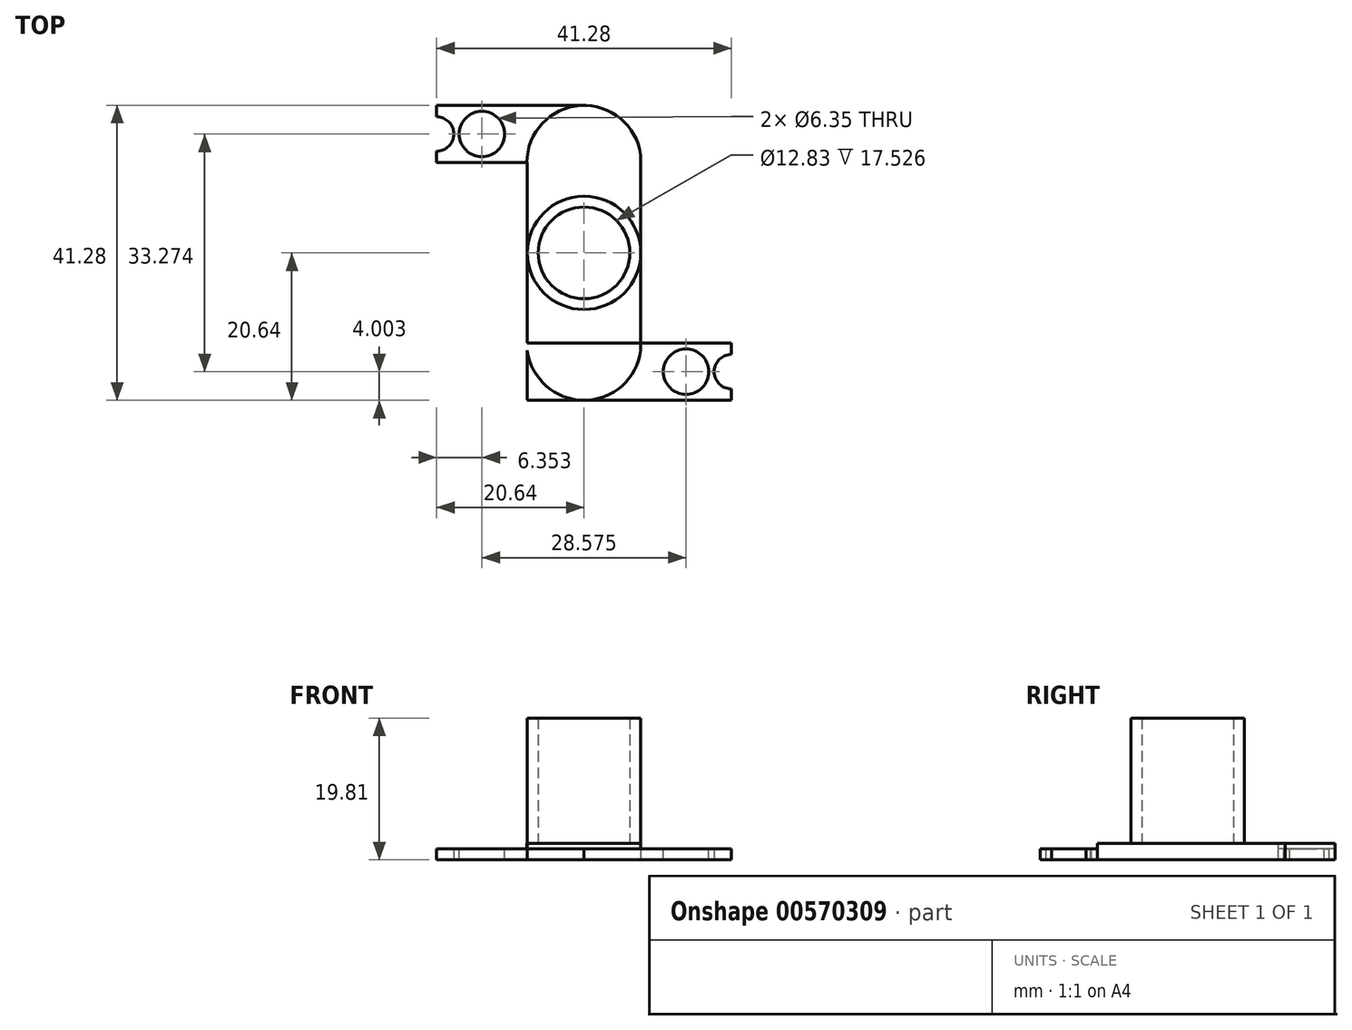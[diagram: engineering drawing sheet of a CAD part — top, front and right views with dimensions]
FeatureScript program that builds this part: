
annotation { "Feature Type Name" : "Feature", "Feature Type Description" : "" }
export const myFeature = defineFeature(function(context is Context, id is Id, definition is map)
    precondition{}
    {
        {
            var Q0;
            Q0=qCreatedBy(makeId("Top.planeOp"),FACE);
            var sketch = newSketch(context, id + "F0", { "sketchPlane" : qUnion([Q0])});
            skLineSegment(sketch, "E0.bottom", {"start": v(20.64, 20.64) * mm, "end": v(-20.64, 20.64) * mm});
            skLineSegment(sketch, "E0.left", {"start": v(20.64, 20.64) * mm, "end": v(20.64, -20.64) * mm});
            skLineSegment(sketch, "E0.right", {"start": v(-20.64, 20.64) * mm, "end": v(-20.64, -20.64) * mm});
            skPoint(sketch, "E0.middle", {"position": v(0, 0) * mm});
            skLineSegment(sketch, "E1.bottom", {"start": v(7.94, 20.64) * mm, "end": v(-7.94, 20.64) * mm});
            skLineSegment(sketch, "E1.top", {"start": v(7.94, -20.64) * mm, "end": v(-7.94, -20.64) * mm});
            skLineSegment(sketch, "E1.left", {"start": v(7.94, 20.64) * mm, "end": v(7.94, -20.64) * mm});
            skLineSegment(sketch, "E1.right", {"start": v(-7.94, 20.64) * mm, "end": v(-7.94, -20.64) * mm});
            skLineSegment(sketch, "E2.bottom", {"start": v(-20.64, 20.64) * mm, "end": v(20.64, 20.64) * mm});
            skLineSegment(sketch, "E2.top", {"start": v(-20.64, 12.64) * mm, "end": v(20.64, 12.64) * mm});
            skLineSegment(sketch, "E2.left", {"start": v(-20.64, 20.64) * mm, "end": v(-20.64, 12.64) * mm});
            skLineSegment(sketch, "E2.right", {"start": v(20.64, 20.64) * mm, "end": v(20.64, 12.64) * mm});
            skLineSegment(sketch, "E3.top", {"start": v(-20.64, -12.64) * mm, "end": v(20.64, -12.64) * mm});
            skLineSegment(sketch, "E3.left", {"start": v(-20.64, -20.64) * mm, "end": v(-20.64, -12.64) * mm});
            skLineSegment(sketch, "E3.right", {"start": v(20.64, -20.64) * mm, "end": v(20.64, -12.64) * mm});
            skArc(sketch, "E4", {"start": v(0, 20.64) * mm, "mid": v(-5.29, 18.64) * mm, "end": v(-7.94, 13.64) * mm});
            skArc(sketch, "E5", {"start": v(0, 20.64) * mm, "mid": v(5.29, 18.64) * mm, "end": v(7.94, 13.64) * mm});
            skArc(sketch, "E6", {"start": v(0, -20.64) * mm, "mid": v(-5.29, -18.64) * mm, "end": v(-7.94, -13.64) * mm});
            skArc(sketch, "E7", {"start": v(0, -20.64) * mm, "mid": v(5.29, -18.64) * mm, "end": v(7.94, -13.64) * mm});
            skLineSegment(sketch, "E8", {"start": v(0, -20.64) * mm, "end": v(20.64, -20.64) * mm});
            skCircle(sketch, "E9", {"center": v(20.64, -16.64) * mm, "radius": 2.41 * mm});
            skCircle(sketch, "E10", {"center": v(-20.64, 16.64) * mm, "radius": 2.41 * mm});
            skSolve(sketch);
        }
        {
            var Q0;
            {var subQ3=sQuery(id+"F0.wireOp",EDGE,"E1.right");var subQ9=sQuery(id+"F0.wireOp",EDGE,"E2.bottom");var subQ10=makeQuery(id+"F0.imprint","INTERSECT",VERTEX,{"derivedFrom":[subQ3,subQ9]});Q0=makeQuery(id+"F0.imprint","IMPRINT",FACE,{"disambiguationData":[TD([[makeQuery(id+"F0.imprint","IMPRINT",EDGE,{"disambiguationData":[TD([[subQ10,-1.0]])],"derivedFrom":subQ3}),-1.0]])]});}
            var Q1;
            {var subQ3=sQuery(id+"F0.wireOp",EDGE,"E4");Q1=makeQuery(id+"F0.imprint","IMPRINT",FACE,{"disambiguationData":[TD([[makeQuery(id+"F0.imprint","IMPRINT",EDGE,{"derivedFrom":subQ3}),-1.0]])]});}
            var Q2;
            {var subQ0=sQuery(id+"F0.wireOp",EDGE,"E4");Q2=makeQuery(id+"F0.imprint","IMPRINT",FACE,{"disambiguationData":[TD([[makeQuery(id+"F0.imprint","IMPRINT",EDGE,{"derivedFrom":subQ0}),1.0]])]});}
            var Q3;
            {var subQ0=sQuery(id+"F0.wireOp",EDGE,"E2.top");var subQ1=sQuery(id+"F0.wireOp",EDGE,"E1.left");var subQ2=makeQuery(id+"F0.imprint","INTERSECT",VERTEX,{"derivedFrom":[subQ1,subQ0]});Q3=makeQuery(id+"F0.imprint","IMPRINT",FACE,{"disambiguationData":[TD([[makeQuery(id+"F0.imprint","IMPRINT",EDGE,{"disambiguationData":[TD([[subQ2,-1.0]])],"derivedFrom":subQ1}),-1.0]])]});}
            var Q4;
            {var subQ0=sQuery(id+"F0.wireOp",EDGE,"E6");Q4=makeQuery(id+"F0.imprint","IMPRINT",FACE,{"disambiguationData":[TD([[makeQuery(id+"F0.imprint","IMPRINT",EDGE,{"derivedFrom":subQ0}),-1.0]])]});}
            var Q5;
            {var subQ3=sQuery(id+"F0.wireOp",EDGE,"E7");Q5=makeQuery(id+"F0.imprint","IMPRINT",FACE,{"disambiguationData":[TD([[makeQuery(id+"F0.imprint","IMPRINT",EDGE,{"derivedFrom":subQ3}),-1.0]])]});}
            var Q6;
            {var subQ7=sQuery(id+"F0.wireOp",EDGE,"E1.left");var subQ10=makeQuery(id+"F0.imprint","INTERSECT",VERTEX,{"derivedFrom":[subQ7,sQuery(id+"F0.wireOp",EDGE,"E7")]});Q6=makeQuery(id+"F0.imprint","IMPRINT",FACE,{"disambiguationData":[TD([[makeQuery(id+"F0.imprint","IMPRINT",EDGE,{"disambiguationData":[TD([[subQ10,1.0]])],"derivedFrom":subQ7}),1.0]])]});}
            extrude(context, id + "F1", {"entities" : qUnion([Q0, Q1, Q2, Q3, Q4, Q5, Q6]), "depth" : 1.52 * mm, "offsetDistance" : 25.4 * mm});
        }
        {
            var Q0;
            Q0=makeQuery(id+"F1.opExtrude","CAP_FACE",FACE,{"disambiguationData":[OSD([sQuery(id+"F0.wireOp",EDGE,"E1.left"),sQuery(id+"F0.wireOp",EDGE,"E1.right"),sQuery(id+"F0.wireOp",EDGE,"E2.bottom"),sQuery(id+"F0.wireOp",EDGE,"E2.top"),sQuery(id+"F0.wireOp",EDGE,"E3.top"),sQuery(id+"F0.wireOp",EDGE,"E3.right"),sQuery(id+"F0.wireOp",EDGE,"E5"),sQuery(id+"F0.wireOp",EDGE,"E6"),sQuery(id+"F0.wireOp",EDGE,"E8"),sQuery(id+"F0.wireOp",EDGE,"E9"),sQuery(id+"F0.wireOp",EDGE,"E2.left"),sQuery(id+"F0.wireOp",EDGE,"E10")])],"isStart":false});
            var sketch = newSketch(context, id + "F2", { "sketchPlane" : qUnion([Q0])});
            skArc(sketch, "E11", {"start": v(0, 20.64) * mm, "mid": v(-5.66, 18.3) * mm, "end": v(-8, 12.64) * mm});
            skArc(sketch, "E12", {"start": v(0, -20.64) * mm, "mid": v(5.66, -18.3) * mm, "end": v(8, -12.64) * mm});
            skSolve(sketch);
        }
        {
            var Q0;
            {var subQ3=sQuery(id+"F2.wireOp",EDGE,"E11");Q0=makeQuery(id+"F2.imprint","IMPRINT",FACE,{"disambiguationData":[TD([[makeQuery(id+"F2.imprint","IMPRINT",EDGE,{"derivedFrom":subQ3}),1.0]])]});}
            extrude(context, id + "F3", {"entities" : qUnion([Q0]), "operationType" : NewBodyOperationType.ADD, "depth" : 0.76 * mm, "offsetDistance" : 25.4 * mm});
        }
        {
            var Q0;
            Q0=makeQuery(id+"F3.opExtrude","CAP_FACE",FACE,{"disambiguationData":[OSD([sQuery(id+"F0.wireOp",EDGE,"E1.left"),sQuery(id+"F0.wireOp",EDGE,"E1.right"),sQuery(id+"F0.wireOp",EDGE,"E2.top"),sQuery(id+"F0.wireOp",EDGE,"E3.top"),sQuery(id+"F0.wireOp",EDGE,"E5"),sQuery(id+"F0.wireOp",EDGE,"E6"),sQuery(id+"F2.wireOp",EDGE,"E11"),sQuery(id+"F2.wireOp",EDGE,"E12")])],"isStart":false});
            var sketch = newSketch(context, id + "F4", { "sketchPlane" : qUnion([Q0])});
            skCircle(sketch, "E13", {"center": v(0, 0) * mm, "radius": 7.94 * mm});
            skCircle(sketch, "E14", {"center": v(0, 0) * mm, "radius": 6.41 * mm});
            skSolve(sketch);
        }
        {
            var Q0;
            Q0=makeQuery(id+"F4.imprint","IMPRINT",FACE,{"disambiguationData":[TD([[makeQuery(id+"F4.imprint","IMPRINT",EDGE,{"derivedFrom":sQuery(id+"F4.wireOp",EDGE,"E14")}),-1.0]])]});
            extrude(context, id + "F5", {"entities" : qUnion([Q0]), "operationType" : NewBodyOperationType.ADD, "depth" : 17.53 * mm, "offsetDistance" : 25.4 * mm});
        }
        {
            var Q0;
            {var subQ0=sQuery(id+"F0.wireOp",EDGE,"E2.left");var subQ1=sQuery(id+"F0.wireOp",EDGE,"E2.bottom");var subQ2=sQuery(id+"F0.wireOp",EDGE,"E10");var subQ3=sQuery(id+"F0.wireOp",EDGE,"E2.top");var subQ4=sQuery(id+"F0.wireOp",EDGE,"E5");Q0=makeQuery(id+"F3.boolean.opBoolean","SPLIT",FACE,{"disambiguationData":[TD([makeQuery(id+"F1.opExtrude","SWEPT_FACE",FACE,{"disambiguationData":[OSD([subQ1])]})])],"derivedFrom":makeQuery(id+"F1.opExtrude","CAP_FACE",FACE,{"disambiguationData":[OSD([sQuery(id+"F0.wireOp",EDGE,"E1.left"),sQuery(id+"F0.wireOp",EDGE,"E1.right"),subQ1,subQ3,sQuery(id+"F0.wireOp",EDGE,"E3.top"),sQuery(id+"F0.wireOp",EDGE,"E3.right"),subQ4,sQuery(id+"F0.wireOp",EDGE,"E6"),sQuery(id+"F0.wireOp",EDGE,"E8"),sQuery(id+"F0.wireOp",EDGE,"E9"),subQ0,subQ2])],"isStart":false})});}
            var sketch = newSketch(context, id + "F6", { "sketchPlane" : qUnion([Q0])});
            skLineSegment(sketch, "E15", {"start": v(-20.64, 20.64) * mm, "end": v(-14.29, 20.64) * mm});
            skLineSegment(sketch, "E16", {"start": v(-14.29, 20.64) * mm, "end": v(-14.29, 12.64) * mm});
            skCircle(sketch, "E17", {"center": v(-14.29, 16.64) * mm, "radius": 3.18 * mm});
            skSolve(sketch);
        }
        {
            var Q0;
            {var subQ7=sQuery(id+"F6.wireOp",EDGE,"E15");Q0=makeQuery(id+"F6.imprint","IMPRINT",FACE,{"disambiguationData":[TD([[makeQuery(id+"F6.imprint","IMPRINT",EDGE,{"derivedFrom":subQ7}),-1.0]])]});}
            var Q1;
            {var subQ0=sQuery(id+"F6.wireOp",EDGE,"E17");var subQ1=sQuery(id+"F6.wireOp",EDGE,"E16");var subQ2=makeQuery(id+"F6.imprint","INTERSECT",VERTEX,{"disambiguationData":[OD(0.0)],"derivedFrom":[subQ1,subQ0]});Q1=makeQuery(id+"F6.imprint","IMPRINT",FACE,{"disambiguationData":[TD([[makeQuery(id+"F6.imprint","IMPRINT",EDGE,{"disambiguationData":[TD([[subQ2,-1.0]])],"derivedFrom":subQ1}),-1.0]])]});}
            var Q2;
            {var subQ0=sQuery(id+"F6.wireOp",EDGE,"E17");var subQ1=sQuery(id+"F6.wireOp",EDGE,"E16");var subQ2=makeQuery(id+"F6.imprint","INTERSECT",VERTEX,{"disambiguationData":[OD(0.0)],"derivedFrom":[subQ1,subQ0]});Q2=makeQuery(id+"F6.imprint","IMPRINT",FACE,{"disambiguationData":[TD([[makeQuery(id+"F6.imprint","IMPRINT",EDGE,{"disambiguationData":[TD([[subQ2,-1.0]])],"derivedFrom":subQ1}),1.0]])]});}
            extrude(context, id + "F7", {"entities" : qUnion([Q0, Q1, Q2]), "operationType" : NewBodyOperationType.REMOVE, "oppositeDirection" : true, "depth" : 25.4 * mm, "offsetDistance" : 25.4 * mm});
        }
        {
            var Q0;
            {var subQ0=sQuery(id+"F0.wireOp",EDGE,"E6");var subQ1=sQuery(id+"F0.wireOp",EDGE,"E3.right");var subQ2=sQuery(id+"F0.wireOp",EDGE,"E3.top");var subQ3=sQuery(id+"F0.wireOp",EDGE,"E9");var subQ4=sQuery(id+"F0.wireOp",EDGE,"E8");Q0=makeQuery(id+"F3.boolean.opBoolean","SPLIT",FACE,{"disambiguationData":[TD([makeQuery(id+"F1.opExtrude","SWEPT_FACE",FACE,{"disambiguationData":[OSD([subQ2])]})])],"derivedFrom":makeQuery(id+"F1.opExtrude","CAP_FACE",FACE,{"disambiguationData":[OSD([sQuery(id+"F0.wireOp",EDGE,"E1.left"),sQuery(id+"F0.wireOp",EDGE,"E1.right"),sQuery(id+"F0.wireOp",EDGE,"E2.bottom"),sQuery(id+"F0.wireOp",EDGE,"E2.top"),subQ2,subQ1,sQuery(id+"F0.wireOp",EDGE,"E5"),subQ0,subQ4,subQ3,sQuery(id+"F0.wireOp",EDGE,"E2.left"),sQuery(id+"F0.wireOp",EDGE,"E10")])],"isStart":false})});}
            var sketch = newSketch(context, id + "F8", { "sketchPlane" : qUnion([Q0])});
            skLineSegment(sketch, "E18", {"start": v(20.64, -20.64) * mm, "end": v(14.29, -20.64) * mm});
            skLineSegment(sketch, "E19", {"start": v(14.29, -20.64) * mm, "end": v(14.29, -12.64) * mm});
            skCircle(sketch, "E20", {"center": v(14.29, -16.64) * mm, "radius": 3.18 * mm});
            skSolve(sketch);
        }
        {
            var Q0;
            {var subQ0=sQuery(id+"F8.wireOp",EDGE,"E20");var subQ1=sQuery(id+"F8.wireOp",EDGE,"E19");var subQ2=makeQuery(id+"F8.imprint","INTERSECT",VERTEX,{"disambiguationData":[OD(0.0)],"derivedFrom":[subQ1,subQ0]});Q0=makeQuery(id+"F8.imprint","IMPRINT",FACE,{"disambiguationData":[TD([[makeQuery(id+"F8.imprint","IMPRINT",EDGE,{"disambiguationData":[TD([[subQ2,-1.0]])],"derivedFrom":subQ1}),1.0]])]});}
            var Q1;
            {var subQ0=sQuery(id+"F8.wireOp",EDGE,"E20");var subQ1=sQuery(id+"F8.wireOp",EDGE,"E19");var subQ2=makeQuery(id+"F8.imprint","INTERSECT",VERTEX,{"disambiguationData":[OD(0.0)],"derivedFrom":[subQ1,subQ0]});Q1=makeQuery(id+"F8.imprint","IMPRINT",FACE,{"disambiguationData":[TD([[makeQuery(id+"F8.imprint","IMPRINT",EDGE,{"disambiguationData":[TD([[subQ2,-1.0]])],"derivedFrom":subQ1}),-1.0]])]});}
            var Q2;
            {var subQ6=sQuery(id+"F8.wireOp",EDGE,"E18");Q2=makeQuery(id+"F8.imprint","IMPRINT",FACE,{"disambiguationData":[TD([[makeQuery(id+"F8.imprint","IMPRINT",EDGE,{"derivedFrom":subQ6}),1.0]])]});}
            extrude(context, id + "F9", {"entities" : qUnion([Q0, Q1, Q2]), "operationType" : NewBodyOperationType.REMOVE, "oppositeDirection" : true, "depth" : 25.4 * mm, "offsetDistance" : 25.4 * mm});
        }
    });
